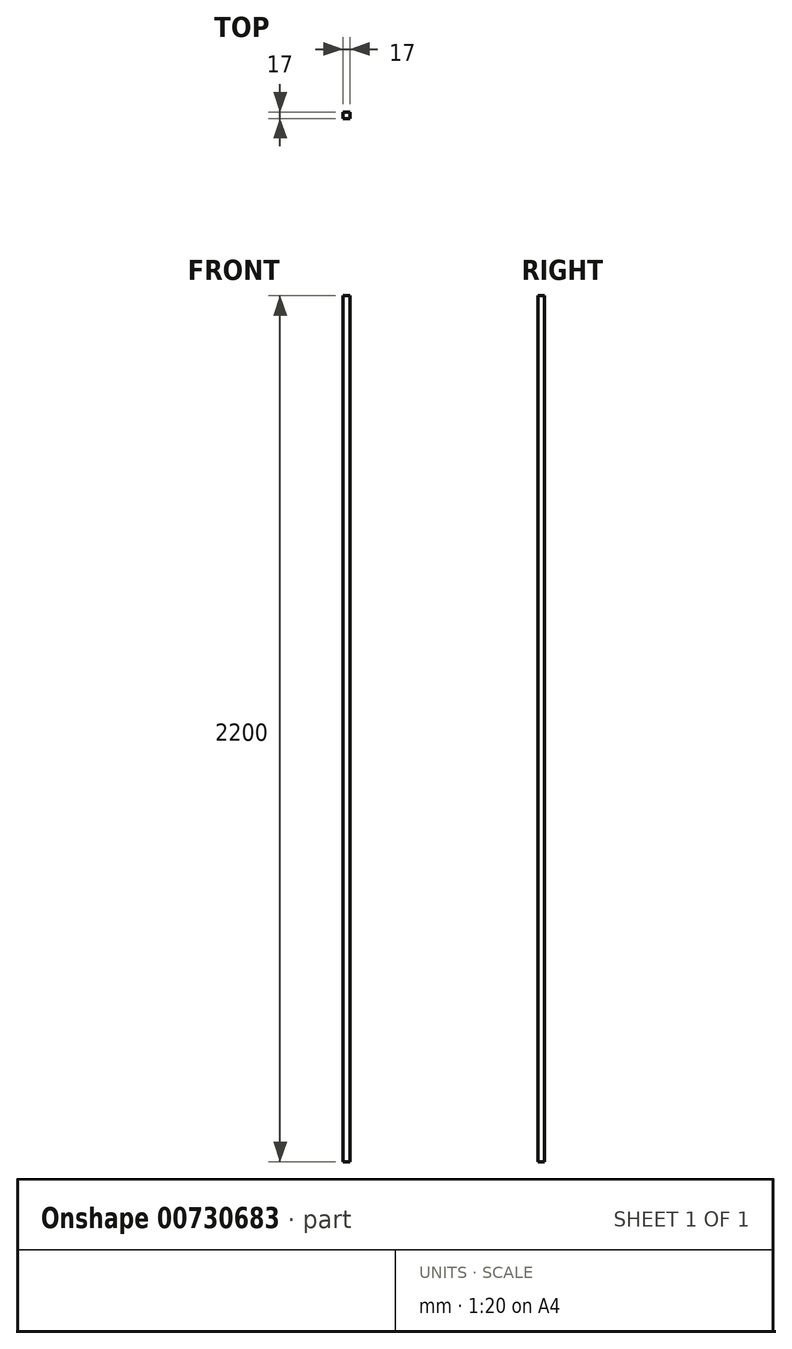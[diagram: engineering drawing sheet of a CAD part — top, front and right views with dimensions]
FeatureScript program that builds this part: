
annotation { "Feature Type Name" : "Feature", "Feature Type Description" : "" }
export const myFeature = defineFeature(function(context is Context, id is Id, definition is map)
    precondition{}
    {
        {
            var Q0;
            Q0=qCreatedBy(makeId("Top.planeOp"),FACE);
            var sketch = newSketch(context, id + "F0", { "sketchPlane" : qUnion([Q0])});
            skLineSegment(sketch, "E0.bottom", {"start": v(0, 0) * mm, "end": v(17, 0) * mm});
            skLineSegment(sketch, "E0.top", {"start": v(0, 17) * mm, "end": v(17, 17) * mm});
            skLineSegment(sketch, "E0.left", {"start": v(0, 0) * mm, "end": v(0, 17) * mm});
            skLineSegment(sketch, "E0.right", {"start": v(17, 0) * mm, "end": v(17, 17) * mm});
            skSolve(sketch);
        }
        {
            var Q0;
            Q0 = qSketchRegion(id + "F0", true);
            extrude(context, id + "F1", {"entities" : qUnion([Q0]), "depth" : 2200 * mm, "offsetDistance" : 25 * mm});
        }
    });
